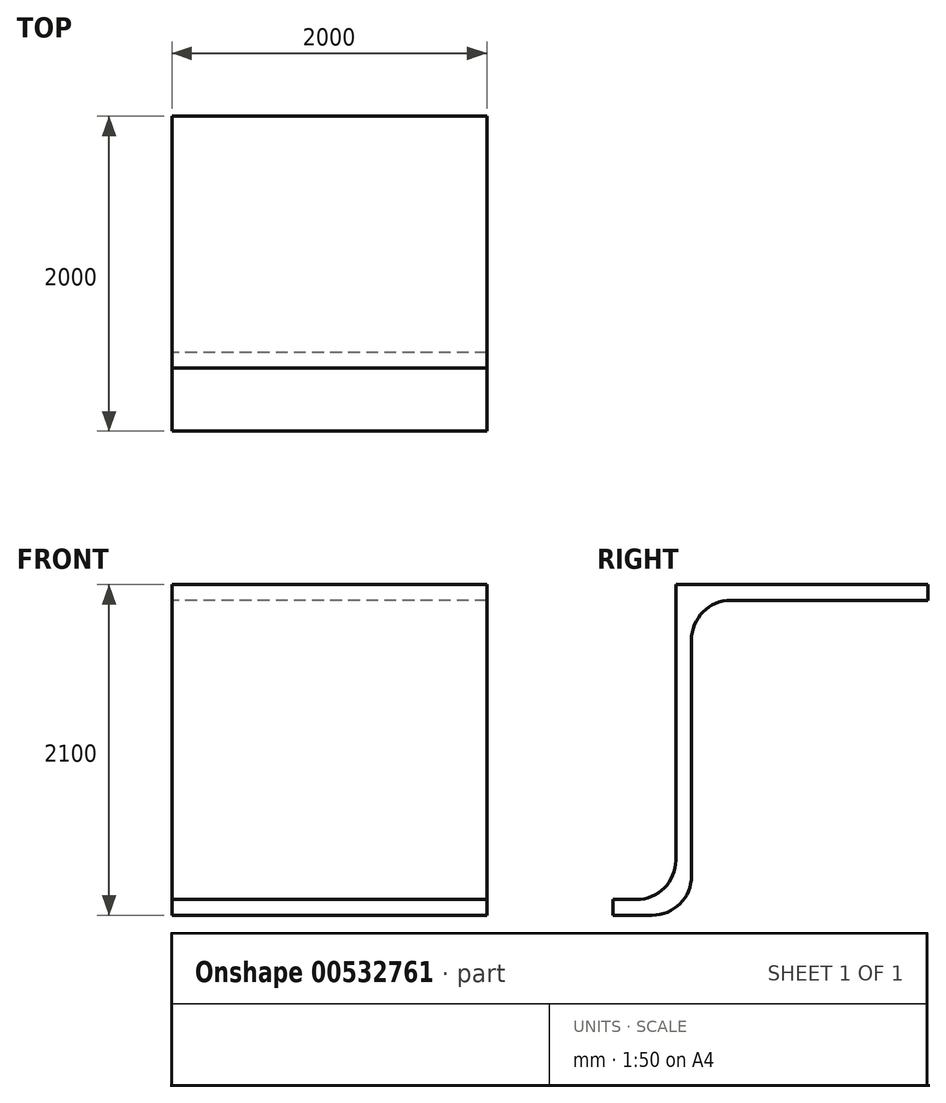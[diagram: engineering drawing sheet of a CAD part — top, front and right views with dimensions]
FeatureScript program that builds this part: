
annotation { "Feature Type Name" : "Feature", "Feature Type Description" : "" }
export const myFeature = defineFeature(function(context is Context, id is Id, definition is map)
    precondition{}
    {
        {
            var Q0;
            Q0=qCreatedBy(makeId("Right.planeOp"),FACE);
            var sketch = newSketch(context, id + "F0", { "sketchPlane" : qUnion([Q0])});
            skLineSegment(sketch, "E0", {"start": v(0, 0) * mm, "end": v(500, 0) * mm});
            skLineSegment(sketch, "E1", {"start": v(500, 0) * mm, "end": v(500, 2000) * mm});
            skLineSegment(sketch, "E2", {"start": v(500, 2000) * mm, "end": v(2000, 2000) * mm});
            skLineSegment(sketch, "E3.0", {"start": v(400, 2100) * mm, "end": v(2000, 2100) * mm});
            skLineSegment(sketch, "E3.1", {"start": v(400, 100) * mm, "end": v(400, 2100) * mm});
            skLineSegment(sketch, "E3.2", {"start": v(0, 100) * mm, "end": v(400, 100) * mm});
            skLineSegment(sketch, "E4", {"start": v(2000, 2100) * mm, "end": v(2000, 2000) * mm});
            skLineSegment(sketch, "E5", {"start": v(0, 100) * mm, "end": v(0, 0) * mm});
            skSolve(sketch);
        }
        {
            var Q0;
            Q0=makeQuery(id+"F0.imprint","IMPRINT",FACE,{"disambiguationData":[TD([[makeQuery(id+"F0.imprint","IMPRINT",EDGE,{"derivedFrom":sQuery(id+"F0.wireOp",EDGE,"E0")}),1.0]])]});
            extrude(context, id + "F1", {"entities" : qUnion([Q0]), "depth" : 2000 * mm, "offsetDistance" : 25 * mm});
        }
        {
            var Q0;
            Q0=makeQuery(id+"F1.opExtrude","SWEPT_EDGE",EDGE,{"disambiguationData":[OSD([sQuery(id+"F0.wireOp",EDGE,"E1"),sQuery(id+"F0.wireOp",EDGE,"E2")])]});
            var Q1;
            Q1=makeQuery(id+"F1.opExtrude","SWEPT_EDGE",EDGE,{"disambiguationData":[OSD([sQuery(id+"F0.wireOp",EDGE,"E0"),sQuery(id+"F0.wireOp",EDGE,"E1")])]});
            var Q2;
            Q2=makeQuery(id+"F1.opExtrude","SWEPT_EDGE",EDGE,{"disambiguationData":[OSD([sQuery(id+"F0.wireOp",EDGE,"E3.1"),sQuery(id+"F0.wireOp",EDGE,"E3.2")])]});
            fillet(context, id + "F2", {"entities" : qUnion([Q0, Q1, Q2]), "radius" : 250 * mm, "tangentPropagation" : true, "allowEdgeOverflow" : false});
        }
    });
